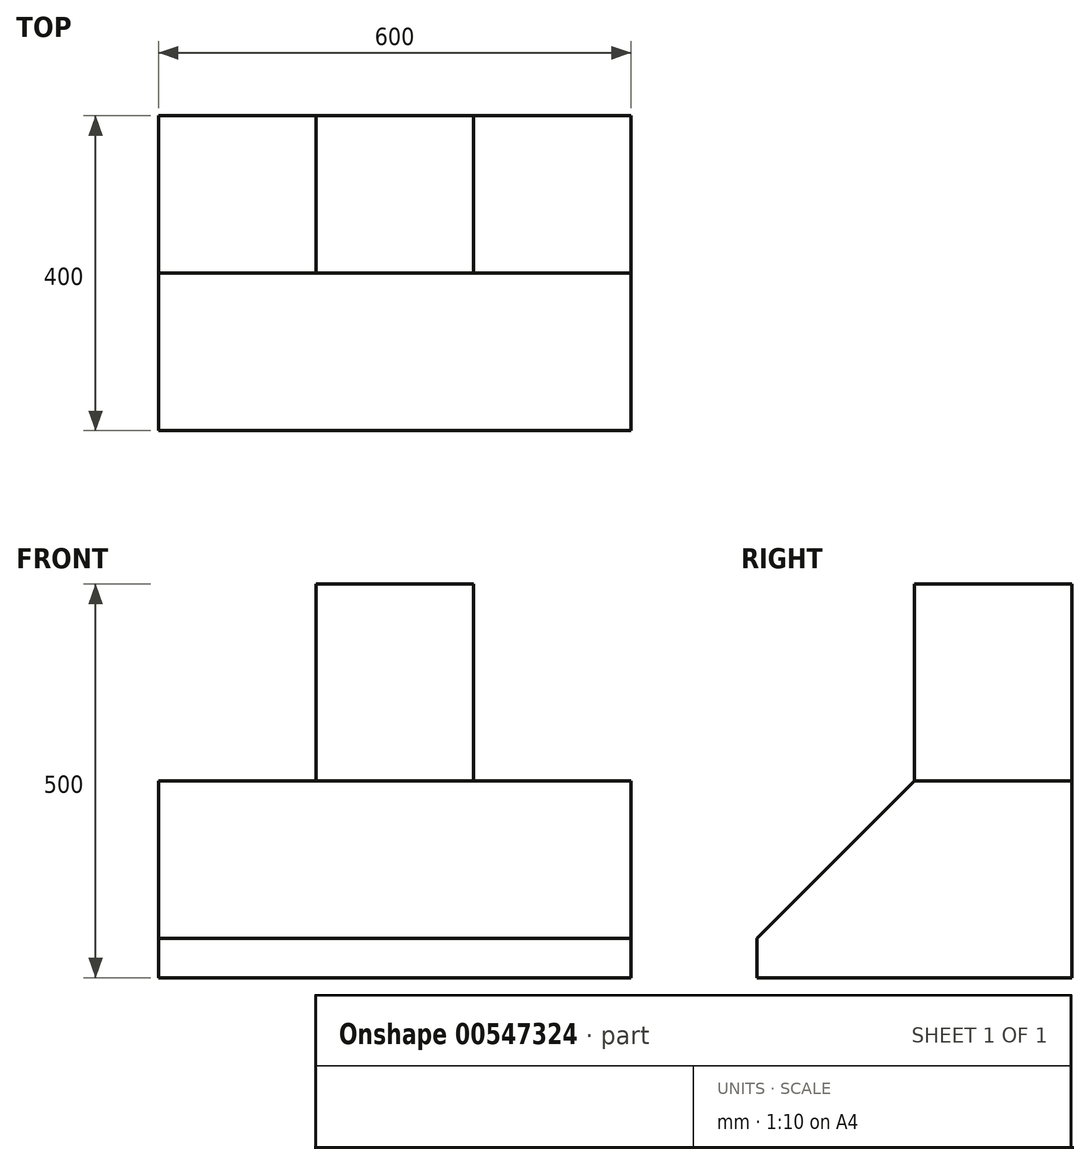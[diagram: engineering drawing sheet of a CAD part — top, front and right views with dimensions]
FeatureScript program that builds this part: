
annotation { "Feature Type Name" : "Feature", "Feature Type Description" : "" }
export const myFeature = defineFeature(function(context is Context, id is Id, definition is map)
    precondition{}
    {
        {
            var Q0;
            Q0=qCreatedBy(makeId("Top.planeOp"),FACE);
            var sketch = newSketch(context, id + "F0", { "sketchPlane" : qUnion([Q0])});
            skLineSegment(sketch, "E0.bottom", {"start": v(300, -200) * mm, "end": v(-300, -200) * mm});
            skLineSegment(sketch, "E0.top", {"start": v(300, 200) * mm, "end": v(-300, 200) * mm});
            skLineSegment(sketch, "E0.left", {"start": v(300, -200) * mm, "end": v(300, 200) * mm});
            skLineSegment(sketch, "E0.right", {"start": v(-300, -200) * mm, "end": v(-300, 200) * mm});
            skPoint(sketch, "E0.middle", {"position": v(0, 0) * mm});
            skSolve(sketch);
        }
        {
            var Q0;
            Q0=makeQuery(id+"F0.imprint","IMPRINT",FACE,{"disambiguationData":[TD([[makeQuery(id+"F0.imprint","IMPRINT",EDGE,{"derivedFrom":sQuery(id+"F0.wireOp",EDGE,"E0.bottom")}),-1.0]])]});
            extrude(context, id + "F1", {"entities" : qUnion([Q0]), "depth" : 250 * mm, "offsetDistance" : 25 * mm});
        }
        {
            var Q0;
            Q0=makeQuery(id+"F1.opExtrude","CAP_FACE",FACE,{"disambiguationData":[OSD([sQuery(id+"F0.wireOp",EDGE,"E0.bottom"),sQuery(id+"F0.wireOp",EDGE,"E0.top"),sQuery(id+"F0.wireOp",EDGE,"E0.left"),sQuery(id+"F0.wireOp",EDGE,"E0.right")])],"isStart":false});
            var sketch = newSketch(context, id + "F2", { "sketchPlane" : qUnion([Q0])});
            skLineSegment(sketch, "E1.bottom", {"start": v(-100, 200) * mm, "end": v(100, 200) * mm});
            skLineSegment(sketch, "E1.top", {"start": v(-100, 0) * mm, "end": v(100, 0) * mm});
            skLineSegment(sketch, "E1.left", {"start": v(-100, 200) * mm, "end": v(-100, 0) * mm});
            skLineSegment(sketch, "E1.right", {"start": v(100, 200) * mm, "end": v(100, 0) * mm});
            skSolve(sketch);
        }
        {
            var Q0;
            Q0=makeQuery(id+"F2.imprint","IMPRINT",FACE,{"disambiguationData":[TD([[makeQuery(id+"F2.imprint","IMPRINT",EDGE,{"derivedFrom":sQuery(id+"F2.wireOp",EDGE,"E1.bottom")}),1.0]])]});
            extrude(context, id + "F3", {"entities" : qUnion([Q0]), "operationType" : NewBodyOperationType.ADD, "depth" : 250 * mm, "offsetDistance" : 25 * mm});
        }
        {
            var Q0;
            Q0=makeQuery(id+"F1.opExtrude","CAP_EDGE",EDGE,{"disambiguationData":[OSD([sQuery(id+"F0.wireOp",EDGE,"E0.bottom")])],"isStart":false});
            chamfer(context, id + "F4", {"entities" : qUnion([Q0]), "width" : 200 * mm, "tangentPropagation" : true});
        }
    });
